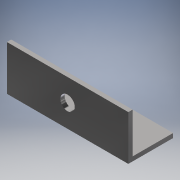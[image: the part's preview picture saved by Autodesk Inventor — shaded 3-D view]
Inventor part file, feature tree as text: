
AUTODESK INVENTOR PART (.ipt)
format: ipt  version: 2017 (Build 210142000, 142)  size: 112,640 bytes
history: native  units: in
note: dims shown in document units (in); Inventor stores cm internally (conversion verified against a paired STEP export)
features: extrude x3, sketch x3
ambient origin geometry x8: Origin, YZ Plane, XZ Plane, XY Plane, X Axis, Y Axis, Z Axis, Center Point
bodies: Solid1 (feature_tree)
feature tree (6):
  extrude  "Extrusion1"  Depth=4.2in
  extrude  "Extrusion2"  Depth=0.15in TaperAngle=0.0deg
  extrude  "Extrusion3"  Depth=1.4in TaperAngle=0.0deg
  sketch  "Sketch1"  dims[d0=1.4in d1=4.2in]
  sketch  "Sketch2"  dims[d2=0.15in d3=0.15in d4=0.0in]
  sketch  "Sketch3"  dims[d5=1.4in d6=0.0in d8=0.6875in d9=0.0in d10=0.375in]
